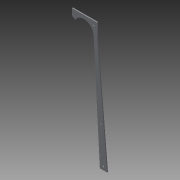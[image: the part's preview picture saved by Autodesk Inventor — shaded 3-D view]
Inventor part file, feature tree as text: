
AUTODESK INVENTOR PART (.ipt)
format: ipt  version: 2013 (Build 170138000, 138)  size: 102,400 bytes
history: native  units: in
note: dims shown in document units (in); Inventor stores cm internally (conversion verified against a paired STEP export)
features: sheet_metal_op x1, sketch x1, other x1
ambient origin geometry x8: Origin, YZ Plane, XZ Plane, XY Plane, X Axis, Y Axis, Z Axis, Center Point
feature tree (3):
  sheet_metal_op  "Face5"
  sketch  "Sketch1"  dims[d0=2.75in d1=30.0deg d2=2.25in d3=1.0in d4=15.5in d5=0.25in d6=0.5in d7=0.5in d10=0.125in d28=0.125in d71=0.125in d72=0.1875in d73=0.1in d74=5.425in d75=0.125in d76=0.25in d77=0.5in d78=0.5in d79=0.125in]
  other  "Plate10"
